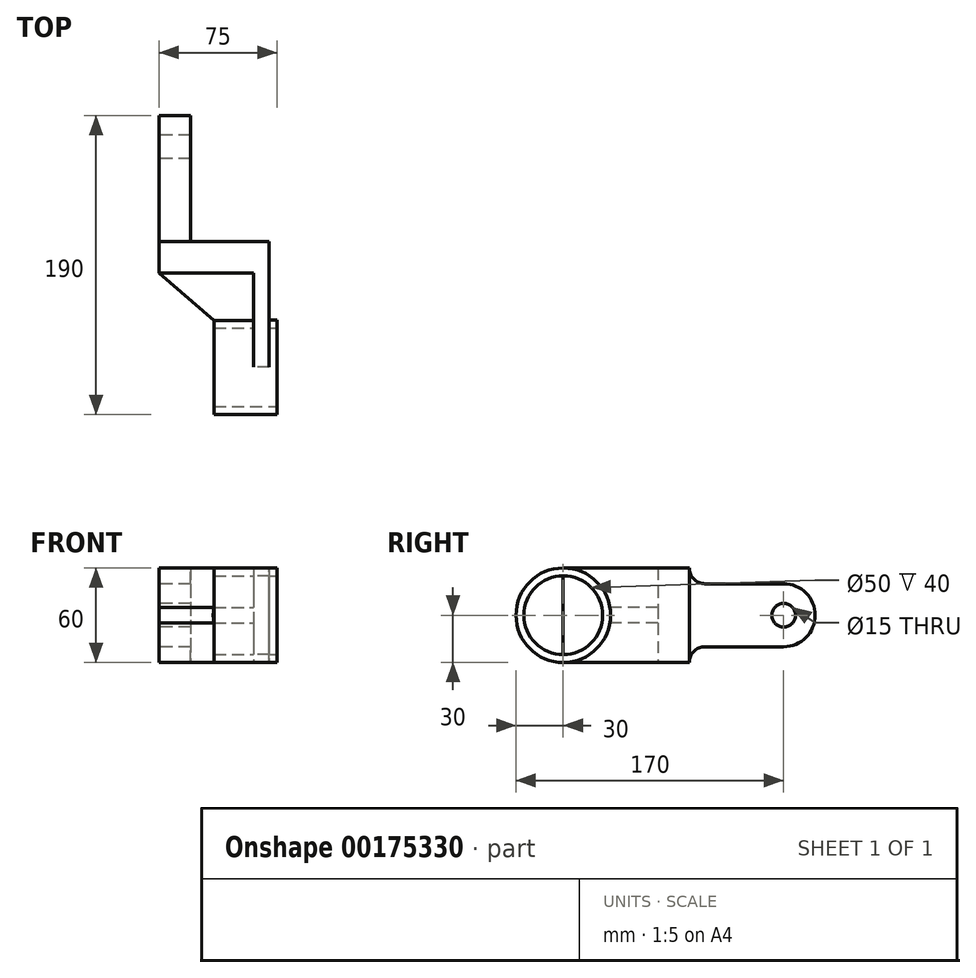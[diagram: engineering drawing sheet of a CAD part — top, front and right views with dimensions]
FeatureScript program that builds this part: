
annotation { "Feature Type Name" : "Feature", "Feature Type Description" : "" }
export const myFeature = defineFeature(function(context is Context, id is Id, definition is map)
    precondition{}
    {
        {
            var Q0;
            Q0=qCreatedBy(makeId("Front.planeOp"),FACE);
            var sketch = newSketch(context, id + "F0", { "sketchPlane" : qUnion([Q0])});
            skLineSegment(sketch, "E0.bottom", {"start": v(-4.95, 60) * mm, "end": v(-74.95, 60) * mm});
            skLineSegment(sketch, "E0.top", {"start": v(-4.95, 0) * mm, "end": v(-74.95, 0) * mm});
            skLineSegment(sketch, "E0.left", {"start": v(-4.95, 60) * mm, "end": v(-4.95, 0) * mm});
            skLineSegment(sketch, "E0.right", {"start": v(-74.95, 60) * mm, "end": v(-74.95, 0) * mm});
            skSolve(sketch);
        }
        {
            var Q0;
            Q0=makeQuery(id+"F0.imprint","IMPRINT",FACE,{"disambiguationData":[TD([[makeQuery(id+"F0.imprint","IMPRINT",EDGE,{"derivedFrom":sQuery(id+"F0.wireOp",EDGE,"E0.bottom")}),1.0]])]});
            extrude(context, id + "F8", {"entities" : qUnion([Q0]), "depth" : 20 * mm});
        }
        {
            var Q0;
            Q0=makeQuery(id+"F8.opExtrude","CAP_FACE",FACE,{"disambiguationData":[OSD([sQuery(id+"F0.wireOp",EDGE,"E0.bottom"),sQuery(id+"F0.wireOp",EDGE,"E0.top"),sQuery(id+"F0.wireOp",EDGE,"E0.left"),sQuery(id+"F0.wireOp",EDGE,"E0.right")])],"isStart":false});
            var sketch = newSketch(context, id + "F1", { "sketchPlane" : qUnion([Q0])});
            skLineSegment(sketch, "E1.bottom", {"start": v(-14.95, 60) * mm, "end": v(-4.95, 60) * mm});
            skLineSegment(sketch, "E1.top", {"start": v(-14.95, 0) * mm, "end": v(-4.95, 0) * mm});
            skLineSegment(sketch, "E1.left", {"start": v(-14.95, 60) * mm, "end": v(-14.95, 0) * mm});
            skLineSegment(sketch, "E1.right", {"start": v(-4.95, 60) * mm, "end": v(-4.95, 0) * mm});
            skSolve(sketch);
        }
        {
            var Q0;
            Q0=makeQuery(id+"F1.imprint","IMPRINT",FACE,{"disambiguationData":[TD([[makeQuery(id+"F1.imprint","IMPRINT",EDGE,{"derivedFrom":sQuery(id+"F1.wireOp",EDGE,"E1.bottom")}),1.0]])]});
            extrude(context, id + "F9", {"entities" : qUnion([Q0]), "operationType" : NewBodyOperationType.ADD, "depth" : 60 * mm});
        }
        {
            var Q0;
            Q0=makeQuery(id+"F9.opExtrude","SWEPT_FACE",FACE,{"disambiguationData":[OSD([sQuery(id+"F1.wireOp",EDGE,"E1.left")])]});
            var sketch = newSketch(context, id + "F2", { "sketchPlane" : qUnion([Q0])});
            skLineSegment(sketch, "E2.bottom", {"start": v(20, 35) * mm, "end": v(80, 35) * mm});
            skLineSegment(sketch, "E2.top", {"start": v(20, 25) * mm, "end": v(80, 25) * mm});
            skLineSegment(sketch, "E2.left", {"start": v(20, 35) * mm, "end": v(20, 25) * mm});
            skLineSegment(sketch, "E2.right", {"start": v(80, 35) * mm, "end": v(80, 25) * mm});
            skCircle(sketch, "E3", {"center": v(80, 30) * mm, "radius": 30 * mm});
            skCircle(sketch, "E4", {"center": v(80, 30) * mm, "radius": 25 * mm});
            skSolve(sketch);
        }
        {
            var Q0;
            {var subQ0=sQuery(id+"F2.wireOp",EDGE,"E3");var subQ1=sQuery(id+"F2.wireOp",EDGE,"E2.bottom");var subQ2=makeQuery(id+"F2.imprint","INTERSECT",VERTEX,{"derivedFrom":[subQ1,subQ0]});Q0=makeQuery(id+"F2.imprint","IMPRINT",FACE,{"disambiguationData":[TD([[makeQuery(id+"F2.imprint","IMPRINT",EDGE,{"disambiguationData":[TD([[subQ2,-1.0]])],"derivedFrom":subQ1}),-1.0]])]});}
            var Q1;
            {var subQ0=sQuery(id+"F2.wireOp",EDGE,"E3");var subQ1=sQuery(id+"F2.wireOp",EDGE,"E2.top");var subQ2=makeQuery(id+"F2.imprint","INTERSECT",VERTEX,{"derivedFrom":[subQ1,subQ0]});Q1=makeQuery(id+"F2.imprint","IMPRINT",FACE,{"disambiguationData":[TD([[makeQuery(id+"F2.imprint","IMPRINT",EDGE,{"disambiguationData":[TD([[subQ2,-1.0]])],"derivedFrom":subQ1}),-1.0]])]});}
            var Q2;
            {var subQ0=sQuery(id+"F2.wireOp",EDGE,"E3");var subQ1=sQuery(id+"F2.wireOp",EDGE,"E2.bottom");var subQ2=makeQuery(id+"F2.imprint","INTERSECT",VERTEX,{"derivedFrom":[subQ1,subQ0]});Q2=makeQuery(id+"F2.imprint","IMPRINT",FACE,{"disambiguationData":[TD([[makeQuery(id+"F2.imprint","IMPRINT",EDGE,{"disambiguationData":[TD([[subQ2,-1.0]])],"derivedFrom":subQ1}),1.0]])]});}
            var Q3;
            {var subQ1=sQuery(id+"F1.wireOp",EDGE,"E1.left");var subQ2=makeQuery(id+"F9.opExtrude","CAP_EDGE",EDGE,{"disambiguationData":[OSD([subQ1])],"isStart":false});var subQ5=sQuery(id+"F2.wireOp",EDGE,"E4");var subQ6=makeQuery(id+"F2.imprint","INTERSECT",VERTEX,{"disambiguationData":[OD(0.0)],"derivedFrom":[subQ2,subQ5]});Q3=makeQuery(id+"F2.imprint","IMPRINT",FACE,{"disambiguationData":[TD([[makeQuery(id+"F2.imprint","IMPRINT",EDGE,{"disambiguationData":[TD([[subQ6,1.0]])],"derivedFrom":subQ5}),-1.0]])]});}
            extrude(context, id + "F10", {"entities" : qUnion([Q0, Q1, Q2, Q3]), "operationType" : NewBodyOperationType.ADD, "depth" : 25 * mm});
        }
        {
            var Q0;
            Q0=makeQuery(id+"F10.opExtrude","CAP_FACE",FACE,{"disambiguationData":[OSD([sQuery(id+"F2.wireOp",EDGE,"E3"),sQuery(id+"F2.wireOp",EDGE,"E4")])],"isStart":false});
            extrude(context, id + "F3", {"entities" : qUnion([Q0]), "operationType" : NewBodyOperationType.ADD, "oppositeDirection" : true, "depth" : 40 * mm});
        }
        {
            var Q0;
            {var subQ0=sQuery(id+"F2.wireOp",EDGE,"E2.left");Q0=makeQuery(id+"F2.imprint","IMPRINT",FACE,{"disambiguationData":[TD([[makeQuery(id+"F2.imprint","IMPRINT",EDGE,{"derivedFrom":subQ0}),1.0]])]});}
            extrude(context, id + "F4", {"entities" : qUnion([Q0]), "operationType" : NewBodyOperationType.ADD, "depth" : 60 * mm});
        }
        {
            var Q0;
            Q0=makeQuery(id+"F4.opExtrude","SWEPT_FACE",FACE,{"disambiguationData":[OSD([sQuery(id+"F2.wireOp",EDGE,"E2.top")])]});
            var sketch = newSketch(context, id + "F5", { "sketchPlane" : qUnion([Q0])});
            skLineSegment(sketch, "E5", {"start": v(-74.95, 20) * mm, "end": v(-39.95, 50.42) * mm});
            skLineSegment(sketch, "E6", {"start": v(-64, 44.37) * mm, "end": v(-64, 44.37) * mm});
            skSolve(sketch);
        }
        {
            var Q0;
            Q0=makeQuery(id+"F5.imprint","IMPRINT",FACE,{"disambiguationData":[TD([[makeQuery(id+"F5.imprint","IMPRINT",EDGE,{"derivedFrom":sQuery(id+"F5.wireOp",EDGE,"E5")}),1.0]])]});
            extrude(context, id + "F11", {"entities" : qUnion([Q0]), "operationType" : NewBodyOperationType.REMOVE, "oppositeDirection" : true, "depth" : 109.89 * mm});
        }
        {
            var Q0;
            Q0=makeQuery(id+"F0.imprint","IMPRINT",FACE,{"disambiguationData":[TD([[makeQuery(id+"F0.imprint","IMPRINT",EDGE,{"derivedFrom":sQuery(id+"F0.wireOp",EDGE,"E0.bottom")}),1.0]])]});
            var sketch = newSketch(context, id + "F6", { "sketchPlane" : qUnion([Q0])});
            skLineSegment(sketch, "E7", {"start": v(-54.95, 60) * mm, "end": v(-54.95, 0) * mm});
            skLineSegment(sketch, "E8", {"start": v(-54.95, 0) * mm, "end": v(-54.95, 0) * mm});
            skSolve(sketch);
        }
        {
            var Q0;
            {var subQ0=sQuery(id+"F6.wireOp",EDGE,"E7");Q0=makeQuery(id+"F6.imprint","IMPRINT",FACE,{"disambiguationData":[TD([[makeQuery(id+"F6.imprint","IMPRINT",EDGE,{"derivedFrom":subQ0}),-1.0]])]});}
            extrude(context, id + "F12", {"entities" : qUnion([Q0]), "operationType" : NewBodyOperationType.ADD, "oppositeDirection" : true, "depth" : 60 * mm});
        }
        {
            var Q0;
            {var subQ0=sQuery(id+"F0.wireOp",EDGE,"E0.right");Q0=makeQuery(id+"F12.boolean.opBoolean","MERGE",FACE,{"derivedFrom":[makeQuery(id+"F4.boolean.opBoolean","MERGE",FACE,{"derivedFrom":[makeQuery(id+"F8.opExtrude","SWEPT_FACE",FACE,{"disambiguationData":[OSD([subQ0])]}),makeQuery(id+"F4.opExtrude","CAP_FACE",FACE,{"disambiguationData":[OSD([sQuery(id+"F2.wireOp",EDGE,"E2.bottom"),sQuery(id+"F2.wireOp",EDGE,"E2.top"),sQuery(id+"F2.wireOp",EDGE,"E2.left"),sQuery(id+"F2.wireOp",EDGE,"E3")])],"isStart":false})]}),makeQuery(id+"F12.opExtrude","SWEPT_FACE",FACE,{"disambiguationData":[OSD([subQ0])]})]});}
            var sketch = newSketch(context, id + "F13", { "sketchPlane" : qUnion([Q0])});
            skArc(sketch, "E9", {"start": v(-20, 60) * mm, "mid": v(-10, 50) * mm, "end": v(0, 60) * mm});
            skPoint(sketch, "E9.endSnap0", {"position": v(-20, 60) * mm});
            skLineSegment(sketch, "E10", {"start": v(-60, 50) * mm, "end": v(-10, 50) * mm});
            skPoint(sketch, "E10.endSnap0", {"position": v(-10, 50) * mm});
            skArc(sketch, "E11", {"start": v(0, 0) * mm, "mid": v(-10, 10) * mm, "end": v(-20, 0) * mm});
            skLineSegment(sketch, "E12", {"start": v(-60, 10) * mm, "end": v(-10, 10) * mm});
            skCircle(sketch, "E13", {"center": v(-60, 30) * mm, "radius": 20 * mm});
            skCircle(sketch, "E14", {"center": v(-60, 30) * mm, "radius": 7.5 * mm});
            skSolve(sketch);
        }
        {
            var Q0;
            {var subQ0=sQuery(id+"F13.wireOp",EDGE,"E9");var subQ5=makeQuery(id+"F13.imprint","INTERSECT",VERTEX,{"derivedFrom":[subQ0,sQuery(id+"F13.wireOp",EDGE,"E10")]});Q0=makeQuery(id+"F13.imprint","IMPRINT",FACE,{"disambiguationData":[TD([[makeQuery(id+"F13.imprint","IMPRINT",EDGE,{"disambiguationData":[TD([[subQ5,1.0]])],"derivedFrom":subQ0}),1.0]])]});}
            var Q1;
            {var subQ5=sQuery(id+"F13.wireOp",EDGE,"E12");Q1=makeQuery(id+"F13.imprint","IMPRINT",FACE,{"disambiguationData":[TD([[makeQuery(id+"F13.imprint","IMPRINT",EDGE,{"derivedFrom":subQ5}),-1.0]])]});}
            var Q2;
            {var subQ0=sQuery(id+"F13.wireOp",EDGE,"E11");var subQ5=makeQuery(id+"F13.imprint","INTERSECT",VERTEX,{"derivedFrom":[subQ0,sQuery(id+"F13.wireOp",EDGE,"E12")]});Q2=makeQuery(id+"F13.imprint","IMPRINT",FACE,{"disambiguationData":[TD([[makeQuery(id+"F13.imprint","IMPRINT",EDGE,{"disambiguationData":[TD([[subQ5,1.0]])],"derivedFrom":subQ0}),1.0]])]});}
            var Q3;
            {var subQ5=sQuery(id+"F13.wireOp",EDGE,"E10");Q3=makeQuery(id+"F13.imprint","IMPRINT",FACE,{"disambiguationData":[TD([[makeQuery(id+"F13.imprint","IMPRINT",EDGE,{"derivedFrom":subQ5}),1.0]])]});}
            var Q4;
            {var subQ0=sQuery(id+"F13.wireOp",EDGE,"E14");var subQ1=makeQuery(id+"F12.opExtrude","CAP_EDGE",EDGE,{"disambiguationData":[OSD([sQuery(id+"F0.wireOp",EDGE,"E0.right")])],"isStart":false});var subQ2=makeQuery(id+"F13.imprint","INTERSECT",VERTEX,{"disambiguationData":[OD(0.0)],"derivedFrom":[subQ1,subQ0]});Q4=makeQuery(id+"F13.imprint","IMPRINT",FACE,{"disambiguationData":[TD([[makeQuery(id+"F13.imprint","IMPRINT",EDGE,{"disambiguationData":[TD([[subQ2,1.0]])],"derivedFrom":subQ0}),1.0]])]});}
            extrude(context, id + "F14", {"entities" : qUnion([Q0, Q1, Q2, Q3, Q4]), "operationType" : NewBodyOperationType.REMOVE, "oppositeDirection" : true, "depth" : 25 * mm});
        }
        {
            var Q0;
            {var subQ1=makeQuery(id+"F12.opExtrude","CAP_EDGE",EDGE,{"disambiguationData":[OSD([sQuery(id+"F0.wireOp",EDGE,"E0.right")])],"isStart":false});var subQ4=sQuery(id+"F13.wireOp",EDGE,"E14");var subQ5=makeQuery(id+"F13.imprint","INTERSECT",VERTEX,{"disambiguationData":[OD(0.0)],"derivedFrom":[subQ1,subQ4]});Q0=makeQuery(id+"F13.imprint","IMPRINT",FACE,{"disambiguationData":[TD([[makeQuery(id+"F13.imprint","IMPRINT",EDGE,{"disambiguationData":[TD([[subQ5,-1.0]])],"derivedFrom":subQ4}),-1.0]])]});}
            var Q1;
            {var subQ1=makeQuery(id+"F12.opExtrude","CAP_EDGE",EDGE,{"disambiguationData":[OSD([sQuery(id+"F0.wireOp",EDGE,"E0.right")])],"isStart":false});var subQ4=sQuery(id+"F13.wireOp",EDGE,"E14");var subQ5=makeQuery(id+"F13.imprint","INTERSECT",VERTEX,{"disambiguationData":[OD(0.0)],"derivedFrom":[subQ1,subQ4]});Q1=makeQuery(id+"F13.imprint","IMPRINT",FACE,{"disambiguationData":[TD([[makeQuery(id+"F13.imprint","IMPRINT",EDGE,{"disambiguationData":[TD([[subQ5,1.0]])],"derivedFrom":subQ4}),-1.0]])]});}
            extrude(context, id + "F7", {"entities" : qUnion([Q0, Q1]), "operationType" : NewBodyOperationType.ADD, "oppositeDirection" : true, "depth" : 20 * mm});
        }
    });
